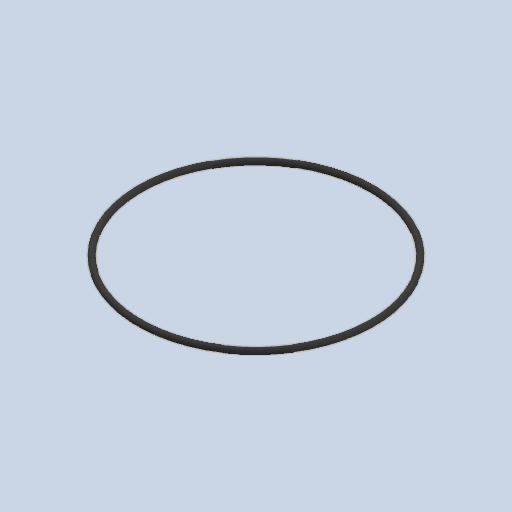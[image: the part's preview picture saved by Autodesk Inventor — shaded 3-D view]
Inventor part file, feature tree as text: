
AUTODESK INVENTOR PART (.ipt)
format: ipt  version: 2024.3 (Build 283343000, 343)  size: 259,072 bytes
history: native  units: mm
features: other x1, revolve x1, sketch x1
ambient origin geometry x8: Origin, YZ Plane, XZ Plane, XY Plane, X Axis, Y Axis, Z Axis, Center Point
bodies: Body1 (feature_tree)
feature tree (3):
  other  "Sólido1"
  revolve  "Revolución1"  Angle=360.0deg
  sketch  "Boceto1"  dims[d0=2.62mm d2=360.0deg d3=44.285mm]
